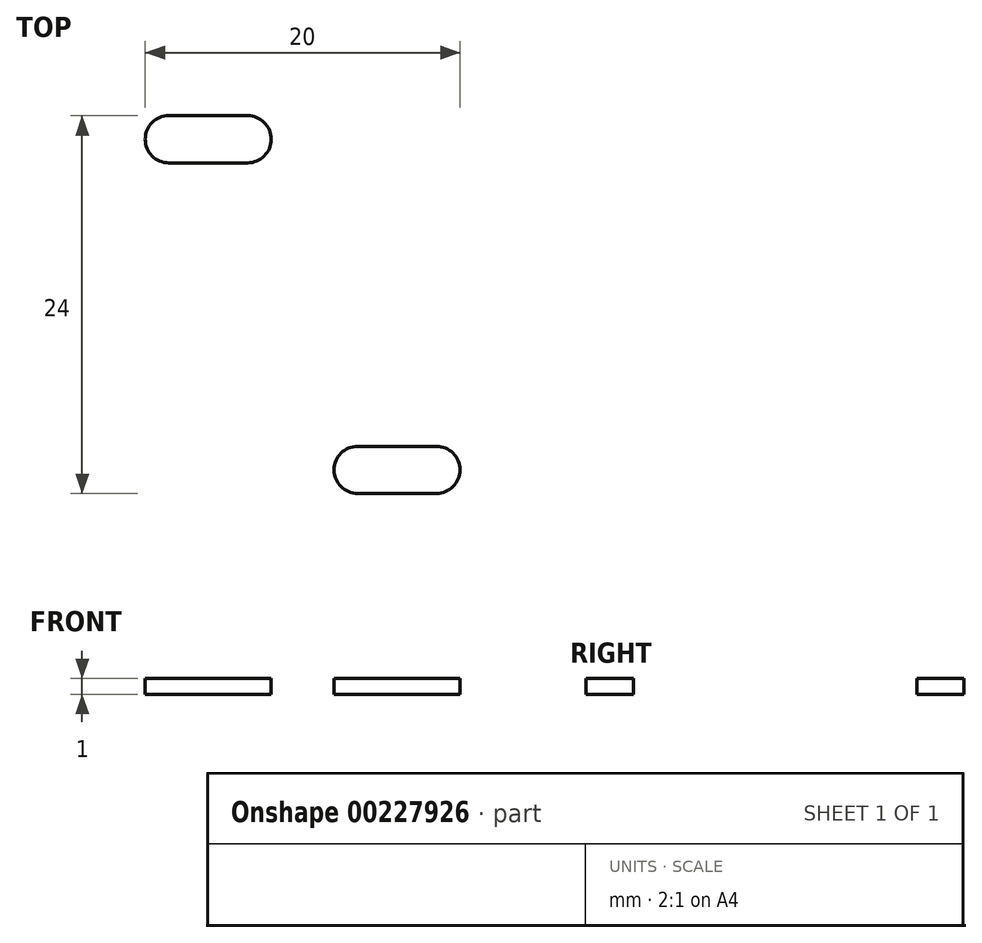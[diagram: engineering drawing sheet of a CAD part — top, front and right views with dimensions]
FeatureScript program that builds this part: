
annotation { "Feature Type Name" : "Feature", "Feature Type Description" : "" }
export const myFeature = defineFeature(function(context is Context, id is Id, definition is map)
    precondition{}
    {
        {
            var Q0;
            Q0=qCreatedBy(makeId("Top.planeOp"),FACE);
            var sketch = newSketch(context, id + "F0", { "sketchPlane" : qUnion([Q0])});
            skLineSegment(sketch, "E0.bottom", {"start": v(-12.5, 15) * mm, "end": v(-9, 15) * mm});
            skLineSegment(sketch, "E0.top", {"start": v(-12.5, -15) * mm, "end": v(-9, -15) * mm});
            skLineSegment(sketch, "E0.left", {"start": v(-12.5, 15) * mm, "end": v(-12.5, -15) * mm});
            skLineSegment(sketch, "E0.right", {"start": v(12.5, 15) * mm, "end": v(12.5, -15) * mm});
            skLineSegment(sketch, "E1", {"start": v(-9, 15) * mm, "end": v(-9, 15.8) * mm});
            skLineSegment(sketch, "E2", {"start": v(-9, 15.8) * mm, "end": v(9, 15.8) * mm});
            skLineSegment(sketch, "E3", {"start": v(9, 15.8) * mm, "end": v(9, 15) * mm});
            skLineSegment(sketch, "E4", {"start": v(9, -15.8) * mm, "end": v(-9, -15.8) * mm});
            skLineSegment(sketch, "E5", {"start": v(-9, -15.8) * mm, "end": v(-9, -15) * mm});
            skLineSegment(sketch, "E6.trimOffspring", {"start": v(9, 15) * mm, "end": v(12.5, 15) * mm});
            skLineSegment(sketch, "E7.trimOffspring", {"start": v(9, -15) * mm, "end": v(9, -15.8) * mm});
            skLineSegment(sketch, "E8.trimOffspring", {"start": v(9, -15) * mm, "end": v(12.5, -15) * mm});
            skLineSegment(sketch, "E9", {"start": v(-12.5, 0) * mm, "end": v(12.5, 0) * mm, "construction": true});
            skLineSegment(sketch, "E10", {"start": v(0, 15.8) * mm, "end": v(0, -15.8) * mm, "construction": true});
            skSolve(sketch);
        }
        {
            var Q0;
            Q0=makeQuery(id+"F0.imprint","IMPRINT",FACE,{"disambiguationData":[TD([[makeQuery(id+"F0.imprint","IMPRINT",EDGE,{"derivedFrom":sQuery(id+"F0.wireOp",EDGE,"E0.bottom")}),-1.0]])]});
            extrude(context, id + "F1", {"entities" : qUnion([Q0]), "depth" : 1 * mm});
        }
        {
            var Q0;
            Q0=makeQuery(id+"F1.opExtrude","CAP_FACE",FACE,{"disambiguationData":[OSD([sQuery(id+"F0.wireOp",EDGE,"E0.bottom"),sQuery(id+"F0.wireOp",EDGE,"E0.top"),sQuery(id+"F0.wireOp",EDGE,"E0.left"),sQuery(id+"F0.wireOp",EDGE,"E0.right"),sQuery(id+"F0.wireOp",EDGE,"E1"),sQuery(id+"F0.wireOp",EDGE,"E2"),sQuery(id+"F0.wireOp",EDGE,"E3"),sQuery(id+"F0.wireOp",EDGE,"E4"),sQuery(id+"F0.wireOp",EDGE,"E5"),sQuery(id+"F0.wireOp",EDGE,"E6.trimOffspring"),sQuery(id+"F0.wireOp",EDGE,"E7.trimOffspring"),sQuery(id+"F0.wireOp",EDGE,"E8.trimOffspring")])],"isStart":false});
            var sketch = newSketch(context, id + "F2", { "sketchPlane" : qUnion([Q0])});
            skArc(sketch, "E11", {"start": v(3.5, 12) * mm, "mid": v(2, 10.5) * mm, "end": v(3.5, 9) * mm});
            skArc(sketch, "E12", {"start": v(8.5, 9) * mm, "mid": v(10, 10.5) * mm, "end": v(8.5, 12) * mm});
            skLineSegment(sketch, "E13", {"start": v(3.5, 12) * mm, "end": v(8.5, 12) * mm});
            skLineSegment(sketch, "E14", {"start": v(3.5, 9) * mm, "end": v(8.5, 9) * mm});
            skArc(sketch, "E15.MirrorCS", {"start": v(-8.5, 9) * mm, "mid": v(-10, 10.5) * mm, "end": v(-8.5, 12) * mm});
            skArc(sketch, "E16.MirrorCS", {"start": v(-3.5, 12) * mm, "mid": v(-2, 10.5) * mm, "end": v(-3.5, 9) * mm});
            skLineSegment(sketch, "E17.MirrorCS", {"start": v(-3.5, 9) * mm, "end": v(-8.5, 9) * mm});
            skLineSegment(sketch, "E18.MirrorCS", {"start": v(-3.5, 12) * mm, "end": v(-8.5, 12) * mm});
            skArc(sketch, "E19.MirrorCS", {"start": v(8.5, -9) * mm, "mid": v(10, -10.5) * mm, "end": v(8.5, -12) * mm});
            skLineSegment(sketch, "E20.MirrorCS", {"start": v(3.5, -12) * mm, "end": v(8.5, -12) * mm});
            skArc(sketch, "E21.MirrorCS", {"start": v(-8.5, -9) * mm, "mid": v(-10, -10.5) * mm, "end": v(-8.5, -12) * mm});
            skLineSegment(sketch, "E22.MirrorCS", {"start": v(-3.5, -9) * mm, "end": v(-8.5, -9) * mm});
            skLineSegment(sketch, "E23.MirrorCS", {"start": v(3.5, -9) * mm, "end": v(8.5, -9) * mm});
            skLineSegment(sketch, "E24.MirrorCS", {"start": v(-3.5, -12) * mm, "end": v(-8.5, -12) * mm});
            skArc(sketch, "E25.MirrorCS", {"start": v(3.5, -12) * mm, "mid": v(2, -10.5) * mm, "end": v(3.5, -9) * mm});
            skArc(sketch, "E26.MirrorCS", {"start": v(-3.5, -12) * mm, "mid": v(-2, -10.5) * mm, "end": v(-3.5, -9) * mm});
            skLineSegment(sketch, "E27.bottom", {"start": v(-8.5, 6) * mm, "end": v(-3.5, 6) * mm});
            skLineSegment(sketch, "E27.top", {"start": v(-8.5, -6) * mm, "end": v(-3.5, -6) * mm});
            skLineSegment(sketch, "E27.left", {"start": v(-10, 4.5) * mm, "end": v(-10, -4.5) * mm});
            skLineSegment(sketch, "E27.right", {"start": v(-2, 4.5) * mm, "end": v(-2, -4.5) * mm});
            skPoint(sketch, "E28.visualSharp", {"position": v(-10, 6) * mm});
            skArc(sketch, "E28.filletArc", {"start": v(-8.5, 6) * mm, "mid": v(-9.56, 5.56) * mm, "end": v(-10, 4.5) * mm});
            skPoint(sketch, "E29.visualSharp", {"position": v(-2, -6) * mm});
            skArc(sketch, "E29.filletArc", {"start": v(-3.5, -6) * mm, "mid": v(-2.44, -5.56) * mm, "end": v(-2, -4.5) * mm});
            skPoint(sketch, "E30.visualSharp", {"position": v(-2, 6) * mm});
            skArc(sketch, "E30.filletArc", {"start": v(-2, 4.5) * mm, "mid": v(-2.44, 5.56) * mm, "end": v(-3.5, 6) * mm});
            skPoint(sketch, "E31.visualSharp", {"position": v(-10, -6) * mm});
            skArc(sketch, "E31.filletArc", {"start": v(-10, -4.5) * mm, "mid": v(-9.56, -5.56) * mm, "end": v(-8.5, -6) * mm});
            skLineSegment(sketch, "E32.MirrorCS", {"start": v(8.5, -6) * mm, "end": v(3.5, -6) * mm});
            skArc(sketch, "E33.MirrorCS", {"start": v(2, 4.5) * mm, "mid": v(2.44, 5.56) * mm, "end": v(3.5, 6) * mm});
            skArc(sketch, "E34.MirrorCS", {"start": v(8.5, 6) * mm, "mid": v(9.56, 5.56) * mm, "end": v(10, 4.5) * mm});
            skPoint(sketch, "E35.MirrorP", {"position": v(10, -6) * mm});
            skPoint(sketch, "E36.MirrorP", {"position": v(2, -6) * mm});
            skLineSegment(sketch, "E37.MirrorCS", {"start": v(8.5, 6) * mm, "end": v(3.5, 6) * mm});
            skLineSegment(sketch, "E38.MirrorCS", {"start": v(10, 4.5) * mm, "end": v(10, -4.5) * mm});
            skLineSegment(sketch, "E39.MirrorCS", {"start": v(2, 4.5) * mm, "end": v(2, -4.5) * mm});
            skPoint(sketch, "E40.MirrorP", {"position": v(10, 6) * mm});
            skPoint(sketch, "E41.MirrorP", {"position": v(2, 6) * mm});
            skArc(sketch, "E42.MirrorCS", {"start": v(3.5, -6) * mm, "mid": v(2.44, -5.56) * mm, "end": v(2, -4.5) * mm});
            skArc(sketch, "E43.MirrorCS", {"start": v(10, -4.5) * mm, "mid": v(9.56, -5.56) * mm, "end": v(8.5, -6) * mm});
            skSolve(sketch);
        }
        {
            var Q0;
            Q0=makeQuery(id+"F2.imprint","IMPRINT",FACE,{"disambiguationData":[TD([[makeQuery(id+"F2.imprint","IMPRINT",EDGE,{"derivedFrom":sQuery(id+"F2.wireOp",EDGE,"E15.MirrorCS")}),-1.0]])]});
            var Q1;
            Q1=makeQuery(id+"F2.imprint","IMPRINT",FACE,{"disambiguationData":[TD([[makeQuery(id+"F2.imprint","IMPRINT",EDGE,{"derivedFrom":sQuery(id+"F2.wireOp",EDGE,"E11")}),1.0]])]});
            var Q2;
            Q2=makeQuery(id+"F2.imprint","IMPRINT",FACE,{"disambiguationData":[TD([[makeQuery(id+"F2.imprint","IMPRINT",EDGE,{"derivedFrom":sQuery(id+"F2.wireOp",EDGE,"E32.MirrorCS")}),-1.0]])]});
            var Q3;
            Q3=makeQuery(id+"F2.imprint","IMPRINT",FACE,{"disambiguationData":[TD([[makeQuery(id+"F2.imprint","IMPRINT",EDGE,{"derivedFrom":sQuery(id+"F2.wireOp",EDGE,"E27.bottom")}),-1.0]])]});
            var Q4;
            Q4=makeQuery(id+"F2.imprint","IMPRINT",FACE,{"disambiguationData":[TD([[makeQuery(id+"F2.imprint","IMPRINT",EDGE,{"derivedFrom":sQuery(id+"F2.wireOp",EDGE,"E21.MirrorCS")}),1.0]])]});
            var Q5;
            Q5=makeQuery(id+"F2.imprint","IMPRINT",FACE,{"disambiguationData":[TD([[makeQuery(id+"F2.imprint","IMPRINT",EDGE,{"derivedFrom":sQuery(id+"F2.wireOp",EDGE,"E19.MirrorCS")}),-1.0]])]});
            extrude(context, id + "F3", {"entities" : qUnion([Q0, Q1, Q2, Q3, Q4, Q5]), "operationType" : NewBodyOperationType.REMOVE, "oppositeDirection" : true, "depth" : 25 * mm});
        }
    });
